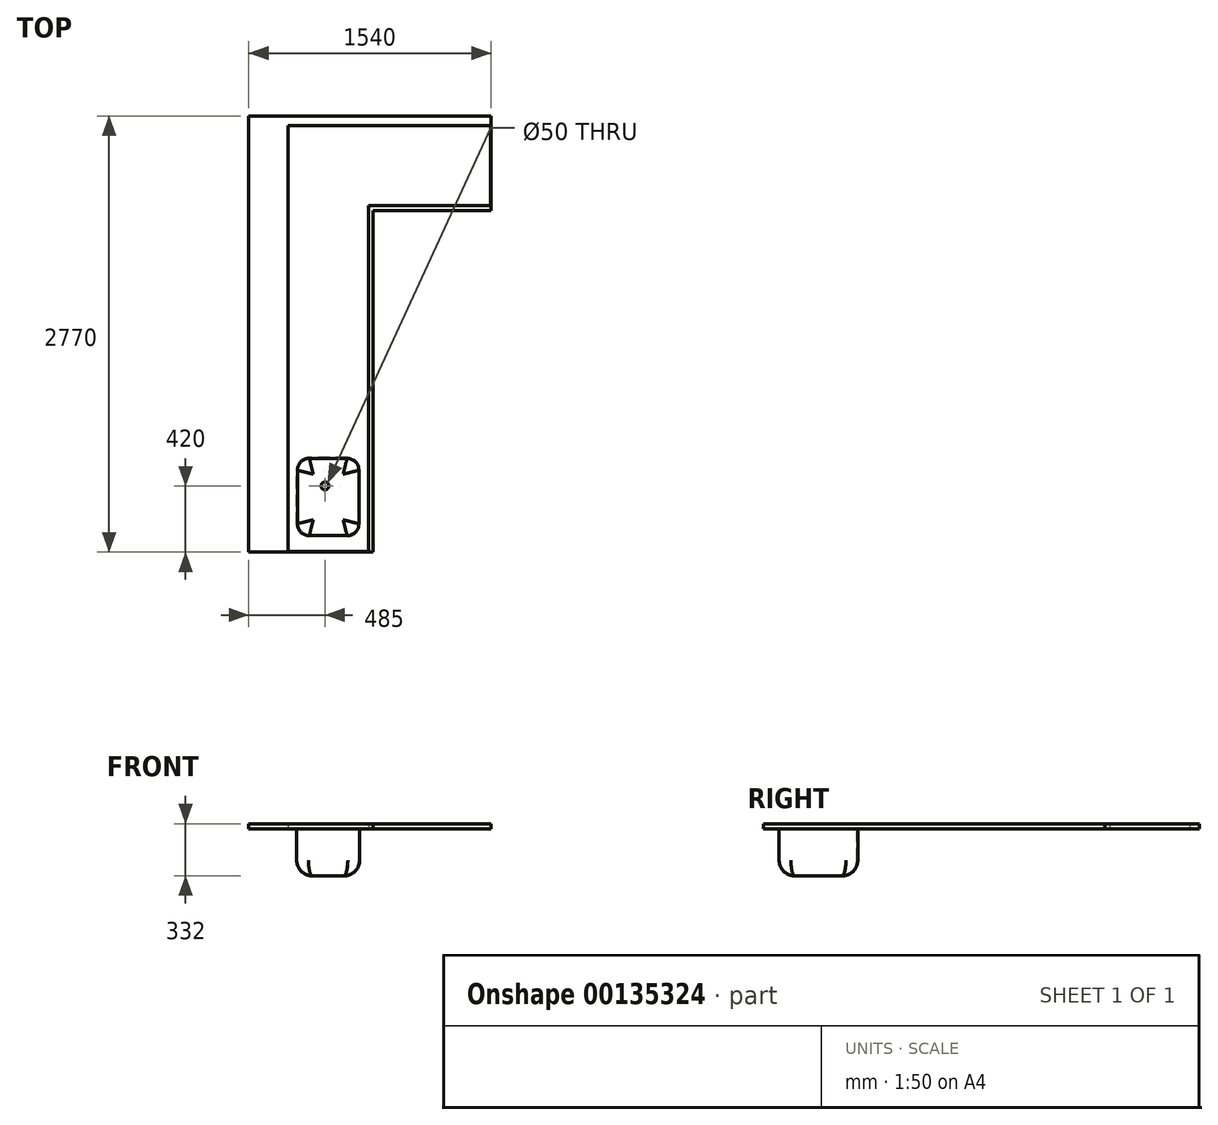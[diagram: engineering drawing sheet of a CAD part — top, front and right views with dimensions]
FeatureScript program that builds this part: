
annotation { "Feature Type Name" : "Feature", "Feature Type Description" : "" }
export const myFeature = defineFeature(function(context is Context, id is Id, definition is map)
    precondition{}
    {
        {
            var Q0;
            Q0=qCreatedBy(makeId("Top.planeOp"),FACE);
            var sketch = newSketch(context, id + "F0", { "sketchPlane" : qUnion([Q0])});
            skLineSegment(sketch, "E0", {"start": v(0, 0) * mm, "end": v(0, 2770) * mm});
            skLineSegment(sketch, "E1", {"start": v(0, 2770) * mm, "end": v(1540, 2770) * mm});
            skLineSegment(sketch, "E2", {"start": v(1540, 2770) * mm, "end": v(1540, 2170) * mm});
            skLineSegment(sketch, "E3", {"start": v(1540, 2170) * mm, "end": v(790, 2170) * mm});
            skLineSegment(sketch, "E4", {"start": v(790, 2170) * mm, "end": v(790, 0) * mm});
            skLineSegment(sketch, "E5", {"start": v(790, 0) * mm, "end": v(0, 0) * mm});
            skSolve(sketch);
        }
        {
            var Q0;
            Q0 = qSketchRegion(id + "F0", true);
            extrude(context, id + "F1", {"entities" : qUnion([Q0]), "depth" : 2 * mm});
        }
        {
            var Q0;
            Q0=makeQuery(id+"F1.opExtrude","CAP_FACE",FACE,{"disambiguationData":[OSD([sQuery(id+"F0.wireOp",EDGE,"E0"),sQuery(id+"F0.wireOp",EDGE,"E1"),sQuery(id+"F0.wireOp",EDGE,"E2"),sQuery(id+"F0.wireOp",EDGE,"E3"),sQuery(id+"F0.wireOp",EDGE,"E4"),sQuery(id+"F0.wireOp",EDGE,"E5")])],"isStart":false});
            var sketch = newSketch(context, id + "F2", { "sketchPlane" : qUnion([Q0])});
            skLineSegment(sketch, "E6", {"start": v(0, 0) * mm, "end": v(0, 2770) * mm});
            skLineSegment(sketch, "E7", {"start": v(0, 2770) * mm, "end": v(1540, 2770) * mm});
            skLineSegment(sketch, "E8", {"start": v(1540, 2770) * mm, "end": v(1540, 2170) * mm});
            skLineSegment(sketch, "E9", {"start": v(1540, 2170) * mm, "end": v(790, 2170) * mm});
            skLineSegment(sketch, "E10", {"start": v(790, 2170) * mm, "end": v(790, 0) * mm});
            skLineSegment(sketch, "E11", {"start": v(790, 0) * mm, "end": v(0, 0) * mm});
            skLineSegment(sketch, "E12", {"start": v(250, 5) * mm, "end": v(250, 2710) * mm});
            skLineSegment(sketch, "E13", {"start": v(250, 2710) * mm, "end": v(1535, 2710) * mm});
            skLineSegment(sketch, "E14", {"start": v(1535, 2710) * mm, "end": v(1535, 2200) * mm});
            skLineSegment(sketch, "E15", {"start": v(1535, 2200) * mm, "end": v(760, 2200) * mm});
            skLineSegment(sketch, "E16", {"start": v(760, 2200) * mm, "end": v(760, 5) * mm});
            skLineSegment(sketch, "E17", {"start": v(760, 5) * mm, "end": v(250, 5) * mm});
            skSolve(sketch);
        }
        {
            var Q0;
            Q0=makeQuery(id+"F2.imprint","IMPRINT",FACE,{"disambiguationData":[TD([[makeQuery(id+"F2.imprint","IMPRINT",EDGE,{"derivedFrom":sQuery(id+"F2.wireOp",EDGE,"E6")}),-1.0]])]});
            extrude(context, id + "F3", {"entities" : qUnion([Q0]), "operationType" : NewBodyOperationType.ADD, "depth" : 30 * mm});
        }
        {
            var Q0;
            Q0=makeQuery(id+"F1.opExtrude","CAP_FACE",FACE,{"disambiguationData":[OSD([sQuery(id+"F0.wireOp",EDGE,"E0"),sQuery(id+"F0.wireOp",EDGE,"E1"),sQuery(id+"F0.wireOp",EDGE,"E2"),sQuery(id+"F0.wireOp",EDGE,"E3"),sQuery(id+"F0.wireOp",EDGE,"E4"),sQuery(id+"F0.wireOp",EDGE,"E5")])],"isStart":true});
            var sketch = newSketch(context, id + "F4", { "sketchPlane" : qUnion([Q0])});
            skLineSegment(sketch, "E18.bottom", {"start": v(705, -100) * mm, "end": v(305, -100) * mm});
            skLineSegment(sketch, "E18.top", {"start": v(705, -600) * mm, "end": v(305, -600) * mm});
            skLineSegment(sketch, "E18.left", {"start": v(705, -100) * mm, "end": v(705, -600) * mm});
            skLineSegment(sketch, "E18.right", {"start": v(305, -100) * mm, "end": v(305, -600) * mm});
            skSolve(sketch);
        }
        {
            var Q0;
            Q0 = qSketchRegion(id + "F4", true);
            extrude(context, id + "F5", {"entities" : qUnion([Q0]), "operationType" : NewBodyOperationType.ADD, "depth" : 300 * mm});
        }
        {
            var Q0;
            Q0=makeQuery(id+"F1.opExtrude","CAP_FACE",FACE,{"disambiguationData":[OSD([sQuery(id+"F0.wireOp",EDGE,"E0"),sQuery(id+"F0.wireOp",EDGE,"E1"),sQuery(id+"F0.wireOp",EDGE,"E2"),sQuery(id+"F0.wireOp",EDGE,"E3"),sQuery(id+"F0.wireOp",EDGE,"E4"),sQuery(id+"F0.wireOp",EDGE,"E5")])],"isStart":false});
            var sketch = newSketch(context, id + "F6", { "sketchPlane" : qUnion([Q0])});
            skLineSegment(sketch, "E19.bottom", {"start": v(385, 105) * mm, "end": v(625, 105) * mm});
            skLineSegment(sketch, "E19.top", {"start": v(385, 595) * mm, "end": v(625, 595) * mm});
            skLineSegment(sketch, "E19.left", {"start": v(310, 180) * mm, "end": v(310, 520) * mm});
            skLineSegment(sketch, "E19.right", {"start": v(700, 180) * mm, "end": v(700, 520) * mm});
            skPoint(sketch, "E20.visualSharp", {"position": v(310, 105) * mm});
            skArc(sketch, "E20.filletArc", {"start": v(310, 180) * mm, "mid": v(331.97, 126.97) * mm, "end": v(385, 105) * mm});
            skPoint(sketch, "E21.visualSharp", {"position": v(310, 595) * mm});
            skArc(sketch, "E21.filletArc", {"start": v(385, 595) * mm, "mid": v(331.97, 573.03) * mm, "end": v(310, 520) * mm});
            skPoint(sketch, "E22.visualSharp", {"position": v(700, 595) * mm});
            skArc(sketch, "E22.filletArc", {"start": v(700, 520) * mm, "mid": v(678.03, 573.03) * mm, "end": v(625, 595) * mm});
            skPoint(sketch, "E23.visualSharp", {"position": v(700, 105) * mm});
            skArc(sketch, "E23.filletArc", {"start": v(625, 105) * mm, "mid": v(678.03, 126.97) * mm, "end": v(700, 180) * mm});
            skSolve(sketch);
        }
        {
            var Q0;
            Q0 = qSketchRegion(id + "F6", true);
            extrude(context, id + "F7", {"entities" : qUnion([Q0]), "operationType" : NewBodyOperationType.REMOVE, "oppositeDirection" : true, "depth" : 300 * mm});
        }
        {
            var Q0;
            Q0=makeQuery(id+"F7.boolean.opBoolean","COPY",EDGE,{"derivedFrom":makeQuery(id+"F7.opExtrude","CAP_EDGE",EDGE,{"disambiguationData":[OSD([sQuery(id+"F6.wireOp",EDGE,"E19.left")])],"isStart":false})});
            fillet(context, id + "F8", {"entities" : qUnion([Q0]), "radius" : 100 * mm, "tangentPropagation" : true, "allowEdgeOverflow" : false});
        }
        {
            var Q0;
            Q0=makeQuery(id+"F5.opExtrude","SWEPT_EDGE",EDGE,{"disambiguationData":[OSD([sQuery(id+"F4.wireOp",EDGE,"E18.bottom"),sQuery(id+"F4.wireOp",EDGE,"E18.left")])]});
            var Q1;
            Q1=makeQuery(id+"F5.opExtrude","SWEPT_EDGE",EDGE,{"disambiguationData":[OSD([sQuery(id+"F4.wireOp",EDGE,"E18.bottom"),sQuery(id+"F4.wireOp",EDGE,"E18.right")])]});
            var Q2;
            Q2=makeQuery(id+"F5.opExtrude","SWEPT_EDGE",EDGE,{"disambiguationData":[OSD([sQuery(id+"F4.wireOp",EDGE,"E18.top"),sQuery(id+"F4.wireOp",EDGE,"E18.left")])]});
            var Q3;
            Q3=makeQuery(id+"F5.opExtrude","SWEPT_EDGE",EDGE,{"disambiguationData":[OSD([sQuery(id+"F4.wireOp",EDGE,"E18.top"),sQuery(id+"F4.wireOp",EDGE,"E18.right")])]});
            fillet(context, id + "F9", {"entities" : qUnion([Q0, Q1, Q2, Q3]), "radius" : 75 * mm, "tangentPropagation" : true, "allowEdgeOverflow" : false});
        }
        {
            var Q0;
            Q0=makeQuery(id+"F5.opExtrude","CAP_EDGE",EDGE,{"disambiguationData":[OSD([sQuery(id+"F4.wireOp",EDGE,"E18.left")])],"isStart":false});
            fillet(context, id + "F10", {"entities" : qUnion([Q0]), "radius" : 100 * mm, "tangentPropagation" : true, "allowEdgeOverflow" : false});
        }
        {
            var Q0;
            Q0=makeQuery(id+"F7.boolean.opBoolean","COPY",FACE,{"derivedFrom":makeQuery(id+"F7.opExtrude","CAP_FACE",FACE,{"disambiguationData":[OSD([sQuery(id+"F6.wireOp",EDGE,"E19.bottom"),sQuery(id+"F6.wireOp",EDGE,"E19.top"),sQuery(id+"F6.wireOp",EDGE,"E19.left"),sQuery(id+"F6.wireOp",EDGE,"E19.right"),sQuery(id+"F6.wireOp",EDGE,"E20.filletArc"),sQuery(id+"F6.wireOp",EDGE,"E21.filletArc"),sQuery(id+"F6.wireOp",EDGE,"E22.filletArc"),sQuery(id+"F6.wireOp",EDGE,"E23.filletArc")])],"isStart":false})});
            var sketch = newSketch(context, id + "F11", { "sketchPlane" : qUnion([Q0])});
            skCircle(sketch, "E24", {"center": v(485, 420) * mm, "radius": 25 * mm});
            skSolve(sketch);
        }
        {
            var Q0;
            Q0 = qSketchRegion(id + "F11", true);
            extrude(context, id + "F12", {"entities" : qUnion([Q0]), "operationType" : NewBodyOperationType.REMOVE, "oppositeDirection" : true, "depth" : 25 * mm, "offsetDistance" : 25 * mm});
        }
    });
